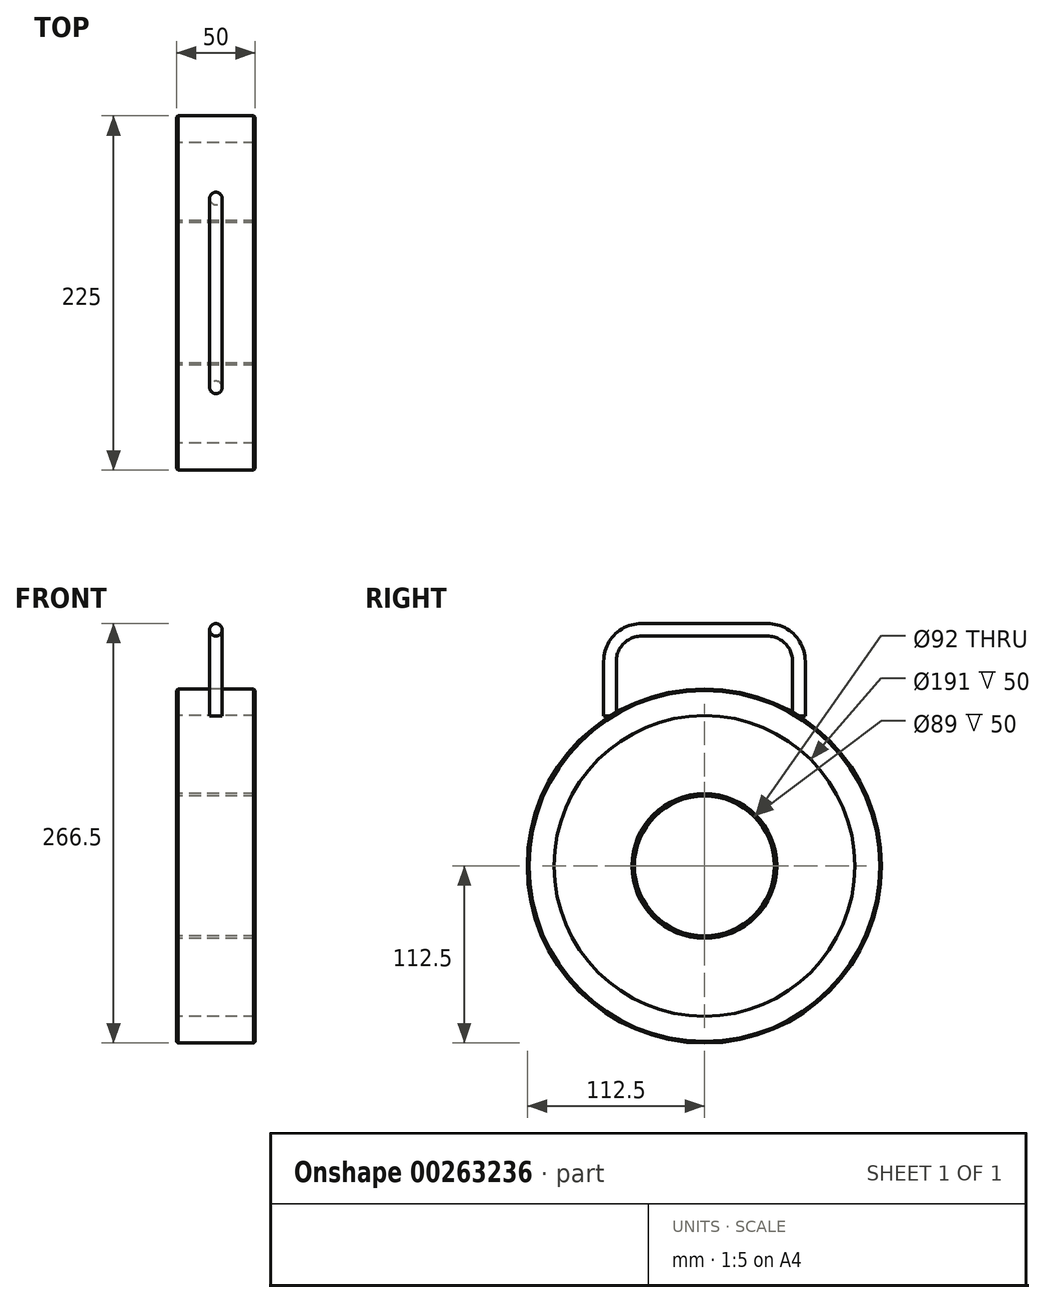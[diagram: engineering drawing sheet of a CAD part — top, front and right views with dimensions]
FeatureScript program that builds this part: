
annotation { "Feature Type Name" : "Feature", "Feature Type Description" : "" }
export const myFeature = defineFeature(function(context is Context, id is Id, definition is map)
    precondition{}
    {
        {
            var Q0;
            Q0=qCreatedBy(makeId("Front.planeOp"),FACE);
            var sketch = newSketch(context, id + "F0", { "sketchPlane" : qUnion([Q0])});
            skLineSegment(sketch, "E0", {"start": v(-38.96, 0) * mm, "end": v(37.1, 0) * mm, "construction": true});
            skLineSegment(sketch, "E1.bottom", {"start": v(-25, 44.5) * mm, "end": v(25, 44.5) * mm});
            skLineSegment(sketch, "E1.top", {"start": v(-25, 46) * mm, "end": v(25, 46) * mm});
            skLineSegment(sketch, "E1.left", {"start": v(-25, 46) * mm, "end": v(-25, 44.5) * mm});
            skLineSegment(sketch, "E1.right", {"start": v(25, 46) * mm, "end": v(25, 44.5) * mm});
            skLineSegment(sketch, "E2", {"start": v(0, 39.63) * mm, "end": v(0, -21.05) * mm, "construction": true});
            skSolve(sketch);
        }
        {
            var Q0;
            Q0 = qSketchRegion(id + "F0", true);
            var Q1;
            Q1=sQuery(id+"F0.wireOp",EDGE,"E0");
            revolve(context, id + "F1", {"entities" : qUnion([Q0]), "axis" : qUnion([Q1]), "revolveType" : RevolveType.FULL});
        }
        {
            var Q0;
            Q0=qCreatedBy(makeId("Front.planeOp"),FACE);
            var sketch = newSketch(context, id + "F2", { "sketchPlane" : qUnion([Q0])});
            skLineSegment(sketch, "E3.top", {"start": v(-25, 95.5) * mm, "end": v(25, 95.5) * mm});
            skLineSegment(sketch, "E3.left", {"start": v(-25, 46) * mm, "end": v(-25, 95.5) * mm});
            skLineSegment(sketch, "E3.right", {"start": v(25, 46) * mm, "end": v(25, 95.5) * mm});
            skLineSegment(sketch, "E4", {"start": v(-38.62, 0) * mm, "end": v(38.62, 0) * mm, "construction": true});
            skLineSegment(sketch, "E5", {"start": v(-25, 46) * mm, "end": v(25, 46) * mm});
            skSolve(sketch);
        }
        {
            var Q0;
            Q0=qCreatedBy(makeId("Front.planeOp"),FACE);
            var sketch = newSketch(context, id + "F3", { "sketchPlane" : qUnion([Q0])});
            skLineSegment(sketch, "E6", {"start": v(-28.54, 0) * mm, "end": v(27.84, 0) * mm, "construction": true});
            skLineSegment(sketch, "E7.bottom", {"start": v(-25, 112.5) * mm, "end": v(25, 112.5) * mm});
            skLineSegment(sketch, "E7.top", {"start": v(-25, 95.5) * mm, "end": v(25, 95.5) * mm});
            skLineSegment(sketch, "E7.left", {"start": v(-25, 112.5) * mm, "end": v(-25, 95.5) * mm});
            skLineSegment(sketch, "E7.right", {"start": v(25, 112.5) * mm, "end": v(25, 95.5) * mm});
            skSolve(sketch);
        }
        {
            var Q0;
            Q0 = qSketchRegion(id + "F2", true);
            var Q1;
            Q1=sQuery(id+"F2.wireOp",EDGE,"E4");
            revolve(context, id + "F4", {"entities" : qUnion([Q0]), "axis" : qUnion([Q1]), "revolveType" : RevolveType.FULL});
        }
        {
            var Q0;
            Q0 = qSketchRegion(id + "F3", true);
            var Q1;
            Q1=sQuery(id+"F0.wireOp",EDGE,"E0");
            revolve(context, id + "F5", {"entities" : qUnion([Q0]), "axis" : qUnion([Q1]), "revolveType" : RevolveType.FULL});
        }
        {
            var Q0;
            Q0=qCreatedBy(makeId("Right.planeOp"),FACE);
            var sketch = newSketch(context, id + "F6", { "sketchPlane" : qUnion([Q0])});
            skLineSegment(sketch, "E8.top", {"start": v(40, 150) * mm, "end": v(-40, 150) * mm});
            skLineSegment(sketch, "E8.left", {"start": v(60, 95.16) * mm, "end": v(60, 130) * mm});
            skLineSegment(sketch, "E8.right", {"start": v(-60, 95.16) * mm, "end": v(-60, 130) * mm});
            skLineSegment(sketch, "E9", {"start": v(0, -49.73) * mm, "end": v(0, 53.43) * mm, "construction": true});
            skLineSegment(sketch, "E10", {"start": v(44.44, 0) * mm, "end": v(-49.73, 0) * mm, "construction": true});
            skArc(sketch, "E11", {"start": v(60, 130) * mm, "mid": v(54.14, 144.14) * mm, "end": v(40, 150) * mm});
            skArc(sketch, "E12", {"start": v(-40, 150) * mm, "mid": v(-54.14, 144.14) * mm, "end": v(-60, 130) * mm});
            skSolve(sketch);
        }
        {
            var Q0;
            Q0=qCreatedBy(makeId("Top.planeOp"),FACE);
            var Q1;
            Q1=sQuery(id+"F6.wireOp",VERTEX,"E8.left.start");
            cPlane(context, id + "F7", {"entities" : qUnion([Q0, Q1]), "cplaneType" : CPlaneType.PLANE_POINT, "offset" : 25 * mm, "width" : 150 * mm, "height" : 150 * mm});
        }
        {
            var Q0;
            Q0=qCreatedBy(id+"F7.planeOp",FACE);
            var sketch = newSketch(context, id + "F8", { "sketchPlane" : qUnion([Q0])});
            skCircle(sketch, "E13", {"center": v(0, 60) * mm, "radius": 4 * mm});
            skSolve(sketch);
        }
        {
            var Q0;
            Q0 = qSketchRegion(id + "F8", true);
            var Q1;
            Q1=sQuery(id+"F6.wireOp",EDGE,"E8.left");
            var Q2;
            Q2=sQuery(id+"F6.wireOp",EDGE,"E11");
            var Q3;
            Q3=sQuery(id+"F6.wireOp",EDGE,"E8.top");
            var Q4;
            Q4=sQuery(id+"F6.wireOp",EDGE,"E12");
            var Q5;
            Q5=sQuery(id+"F6.wireOp",EDGE,"E8.right");
            sweep(context, id + "F9", {"profiles" : qUnion([Q0]), "path" : qUnion([Q1, Q2, Q3, Q4, Q5])});
        }
        {
            var Q0;
            Q0=makeQuery(id+"F5.opRevolve","SWEPT_EDGE",EDGE,{"disambiguationData":[OSD([sQuery(id+"F3.wireOp",EDGE,"E7.bottom"),sQuery(id+"F3.wireOp",EDGE,"E7.right")])]});
            var Q1;
            Q1=makeQuery(id+"F5.opRevolve","SWEPT_EDGE",EDGE,{"disambiguationData":[OSD([sQuery(id+"F3.wireOp",EDGE,"E7.bottom"),sQuery(id+"F3.wireOp",EDGE,"E7.left")])]});
            chamfer(context, id + "F10", {"entities" : qUnion([Q0, Q1]), "width" : 1 * mm, "tangentPropagation" : true});
        }
    });
